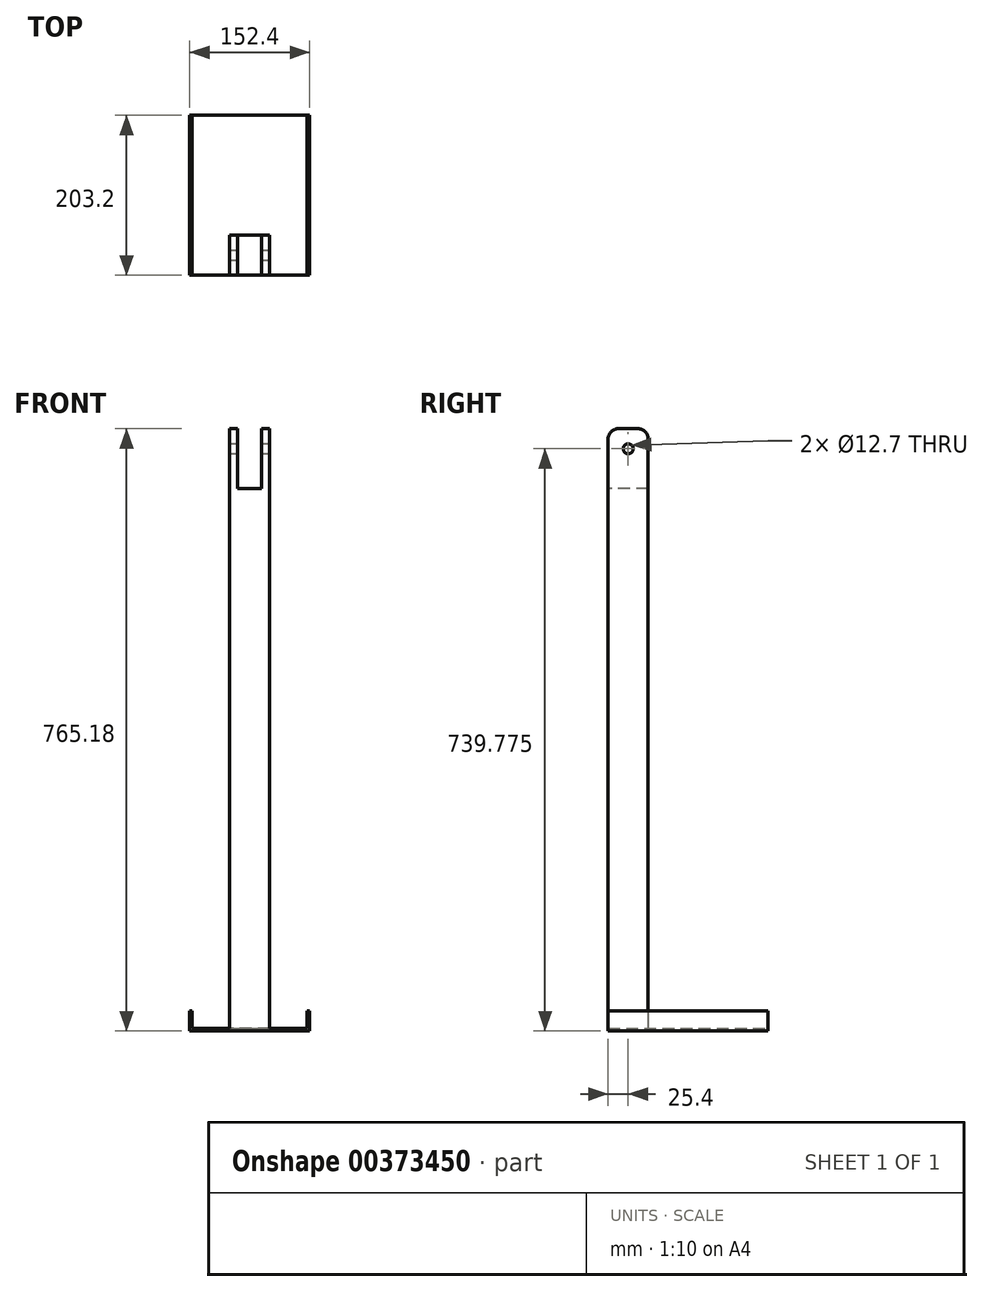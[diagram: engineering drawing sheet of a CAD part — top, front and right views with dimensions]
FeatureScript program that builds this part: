
annotation { "Feature Type Name" : "Feature", "Feature Type Description" : "" }
export const myFeature = defineFeature(function(context is Context, id is Id, definition is map)
    precondition{}
    {
        {
            var Q0;
            Q0=qCreatedBy(makeId("Front.planeOp"),FACE);
            var sketch = newSketch(context, id + "F0", { "sketchPlane" : qUnion([Q0])});
            skLineSegment(sketch, "E0", {"start": v(-76.2, 25.4) * mm, "end": v(-76.2, 0) * mm});
            skLineSegment(sketch, "E1", {"start": v(-76.2, 0) * mm, "end": v(76.2, 0) * mm});
            skLineSegment(sketch, "E2", {"start": v(76.2, 0) * mm, "end": v(76.2, 25.4) * mm});
            skLineSegment(sketch, "E3.0", {"start": v(73.03, 3.17) * mm, "end": v(73.03, 25.4) * mm});
            skLineSegment(sketch, "E3.1", {"start": v(-73.03, 3.17) * mm, "end": v(73.03, 3.17) * mm});
            skLineSegment(sketch, "E3.2", {"start": v(-73.03, 25.4) * mm, "end": v(-73.03, 3.17) * mm});
            skLineSegment(sketch, "E4", {"start": v(-76.2, 25.4) * mm, "end": v(-73.03, 25.4) * mm});
            skLineSegment(sketch, "E5", {"start": v(73.03, 25.4) * mm, "end": v(76.2, 25.4) * mm});
            skSolve(sketch);
        }
        {
            var Q0;
            Q0 = qSketchRegion(id + "F0", true);
            extrude(context, id + "F1", {"entities" : qUnion([Q0]), "endBound" : BoundingType.SYMMETRIC, "depth" : 203.2 * mm});
        }
        {
            var Q0;
            Q0=makeQuery(id+"F1.opExtrude","SWEPT_FACE",FACE,{"disambiguationData":[OSD([sQuery(id+"F0.wireOp",EDGE,"E3.1")])]});
            var sketch = newSketch(context, id + "F2", { "sketchPlane" : qUnion([Q0])});
            skLineSegment(sketch, "E6.bottom", {"start": v(25.4, -101.6) * mm, "end": v(-25.4, -101.6) * mm});
            skLineSegment(sketch, "E6.top", {"start": v(25.4, -50.8) * mm, "end": v(-25.4, -50.8) * mm});
            skLineSegment(sketch, "E6.left", {"start": v(25.4, -101.6) * mm, "end": v(25.4, -50.8) * mm});
            skLineSegment(sketch, "E6.right", {"start": v(-25.4, -101.6) * mm, "end": v(-25.4, -50.8) * mm});
            skPoint(sketch, "E6.middle", {"position": v(0, -70.17) * mm});
            skPoint(sketch, "E7", {"position": v(0, -101.6) * mm});
            skSolve(sketch);
        }
        {
            var Q0;
            Q0 = qSketchRegion(id + "F2", true);
            extrude(context, id + "F3", {"entities" : qUnion([Q0]), "operationType" : NewBodyOperationType.ADD, "depth" : 762 * mm});
        }
        {
            var Q0;
            Q0=makeQuery(id+"F3.opExtrude","SWEPT_FACE",FACE,{"disambiguationData":[OSD([sQuery(id+"F2.wireOp",EDGE,"E6.left")])]});
            var sketch = newSketch(context, id + "F4", { "sketchPlane" : qUnion([Q0])});
            skCircle(sketch, "E8", {"center": v(-76.2, 739.78) * mm, "radius": 6.35 * mm});
            skPoint(sketch, "E8.centerSnap0", {"position": v(-76.2, 765.18) * mm});
            skSolve(sketch);
        }
        {
            var Q0;
            Q0 = qSketchRegion(id + "F4", true);
            extrude(context, id + "F5", {"entities" : qUnion([Q0]), "operationType" : NewBodyOperationType.REMOVE, "endBound" : BoundingType.THROUGH_ALL, "oppositeDirection" : true, "depth" : 25.4 * mm});
        }
        {
            var Q0;
            Q0=makeQuery(id+"F3.boolean.opBoolean","MERGE",FACE,{"derivedFrom":[makeQuery(id+"F1.opExtrude","CAP_FACE",FACE,{"disambiguationData":[OSD([sQuery(id+"F0.wireOp",EDGE,"E0"),sQuery(id+"F0.wireOp",EDGE,"E1"),sQuery(id+"F0.wireOp",EDGE,"E2"),sQuery(id+"F0.wireOp",EDGE,"E3.0"),sQuery(id+"F0.wireOp",EDGE,"E3.1"),sQuery(id+"F0.wireOp",EDGE,"E3.2"),sQuery(id+"F0.wireOp",EDGE,"E4"),sQuery(id+"F0.wireOp",EDGE,"E5")])],"isStart":false}),makeQuery(id+"F3.opExtrude","SWEPT_FACE",FACE,{"disambiguationData":[OSD([sQuery(id+"F2.wireOp",EDGE,"E6.bottom")])]})]});
            var sketch = newSketch(context, id + "F6", { "sketchPlane" : qUnion([Q0])});
            skLineSegment(sketch, "E9.bottom", {"start": v(-15.24, 765.18) * mm, "end": v(15.24, 765.18) * mm});
            skLineSegment(sketch, "E9.top", {"start": v(-15.24, 688.98) * mm, "end": v(15.24, 688.98) * mm});
            skLineSegment(sketch, "E9.left", {"start": v(-15.24, 765.18) * mm, "end": v(-15.24, 688.98) * mm});
            skLineSegment(sketch, "E9.right", {"start": v(15.24, 765.18) * mm, "end": v(15.24, 688.98) * mm});
            skSolve(sketch);
        }
        {
            var Q0;
            Q0 = qSketchRegion(id + "F6", true);
            extrude(context, id + "F7", {"entities" : qUnion([Q0]), "operationType" : NewBodyOperationType.REMOVE, "endBound" : BoundingType.THROUGH_ALL, "oppositeDirection" : true, "depth" : 25.4 * mm});
        }
        {
            var Q0;
            {var subQ0=sQuery(id+"F2.wireOp",EDGE,"E6.right");var subQ1=sQuery(id+"F2.wireOp",EDGE,"E6.bottom");Q0=makeQuery(id+"F7.boolean.opBoolean","SPLIT",EDGE,{"disambiguationData":[TD([makeQuery(id+"F3.opExtrude","SWEPT_FACE",FACE,{"disambiguationData":[OSD([subQ0])]})])],"derivedFrom":makeQuery(id+"F3.opExtrude","CAP_EDGE",EDGE,{"disambiguationData":[OSD([subQ1])],"isStart":false})});}
            var Q1;
            {var subQ0=sQuery(id+"F2.wireOp",EDGE,"E6.right");var subQ1=sQuery(id+"F2.wireOp",EDGE,"E6.top");Q1=makeQuery(id+"F7.boolean.opBoolean","SPLIT",EDGE,{"disambiguationData":[TD([makeQuery(id+"F3.opExtrude","SWEPT_FACE",FACE,{"disambiguationData":[OSD([subQ0])]})])],"derivedFrom":makeQuery(id+"F3.opExtrude","CAP_EDGE",EDGE,{"disambiguationData":[OSD([subQ1])],"isStart":false})});}
            var Q2;
            {var subQ0=sQuery(id+"F2.wireOp",EDGE,"E6.left");var subQ1=sQuery(id+"F2.wireOp",EDGE,"E6.top");Q2=makeQuery(id+"F7.boolean.opBoolean","SPLIT",EDGE,{"disambiguationData":[TD([makeQuery(id+"F3.opExtrude","SWEPT_FACE",FACE,{"disambiguationData":[OSD([subQ0])]})])],"derivedFrom":makeQuery(id+"F3.opExtrude","CAP_EDGE",EDGE,{"disambiguationData":[OSD([subQ1])],"isStart":false})});}
            var Q3;
            {var subQ0=sQuery(id+"F2.wireOp",EDGE,"E6.left");var subQ1=sQuery(id+"F2.wireOp",EDGE,"E6.bottom");Q3=makeQuery(id+"F7.boolean.opBoolean","SPLIT",EDGE,{"disambiguationData":[TD([makeQuery(id+"F3.opExtrude","SWEPT_FACE",FACE,{"disambiguationData":[OSD([subQ0])]})])],"derivedFrom":makeQuery(id+"F3.opExtrude","CAP_EDGE",EDGE,{"disambiguationData":[OSD([subQ1])],"isStart":false})});}
            fillet(context, id + "F8", {"entities" : qUnion([Q0, Q1, Q2, Q3]), "radius" : 12.7 * mm, "tangentPropagation" : true, "allowEdgeOverflow" : false});
        }
    });
